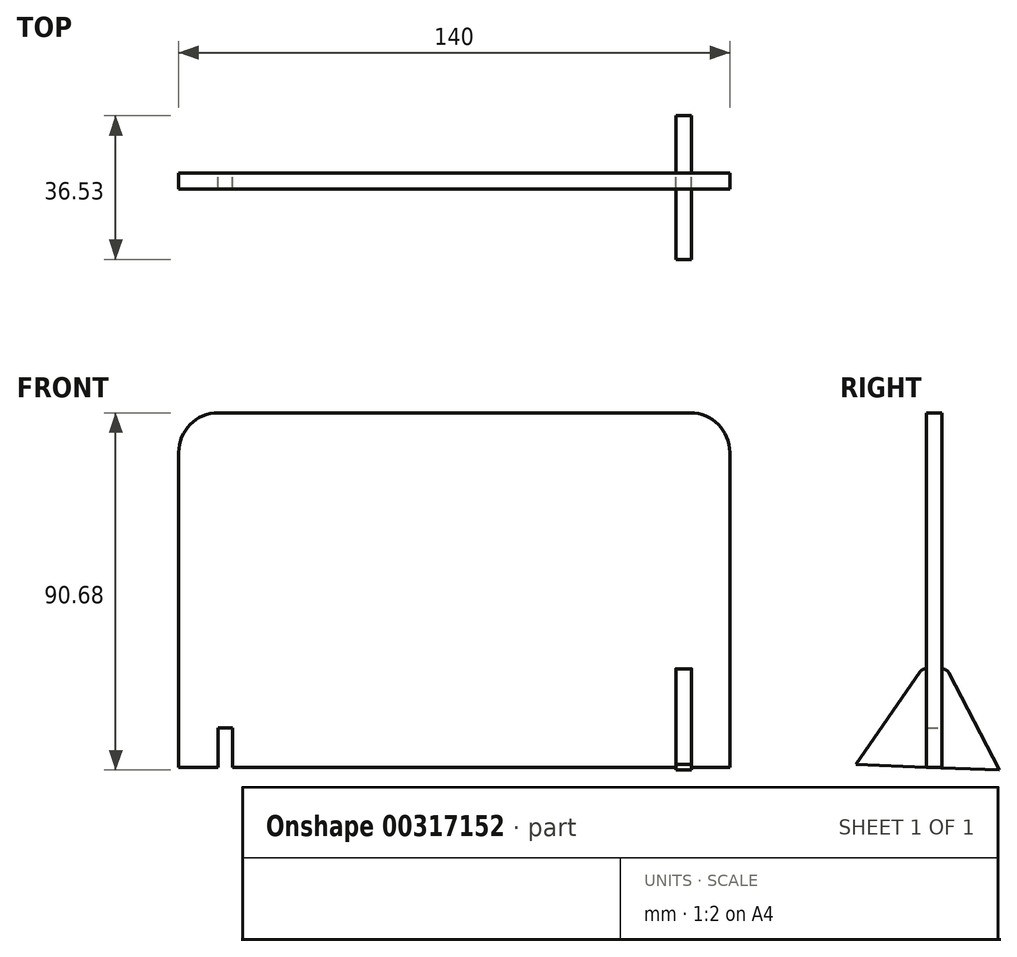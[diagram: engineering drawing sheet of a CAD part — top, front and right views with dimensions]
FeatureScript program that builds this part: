
annotation { "Feature Type Name" : "Feature", "Feature Type Description" : "" }
export const myFeature = defineFeature(function(context is Context, id is Id, definition is map)
    precondition{}
    {
        {
            var Q0;
            Q0=qCreatedBy(makeId("Front.planeOp"),FACE);
            var sketch = newSketch(context, id + "F0", { "sketchPlane" : qUnion([Q0])});
            skLineSegment(sketch, "E0.bottom", {"start": v(-60, 90) * mm, "end": v(60, 90) * mm});
            skLineSegment(sketch, "E0.top", {"start": v(-70, 0) * mm, "end": v(-60, 0) * mm});
            skLineSegment(sketch, "E0.left", {"start": v(-70, 80) * mm, "end": v(-70, 0) * mm});
            skLineSegment(sketch, "E0.right", {"start": v(70, 80) * mm, "end": v(70, 0) * mm});
            skPoint(sketch, "E1.visualSharp", {"position": v(-70, 90) * mm});
            skArc(sketch, "E1.filletArc", {"start": v(-60, 90) * mm, "mid": v(-67.07, 87.07) * mm, "end": v(-70, 80) * mm});
            skPoint(sketch, "E2.visualSharp", {"position": v(70, 90) * mm});
            skArc(sketch, "E2.filletArc", {"start": v(70, 80) * mm, "mid": v(67.07, 87.07) * mm, "end": v(60, 90) * mm});
            skLineSegment(sketch, "E3.top", {"start": v(-60, 10) * mm, "end": v(-56.3, 10) * mm});
            skLineSegment(sketch, "E3.left", {"start": v(-60, 0) * mm, "end": v(-60, 10) * mm});
            skLineSegment(sketch, "E3.right", {"start": v(-56.3, 0) * mm, "end": v(-56.3, 10) * mm});
            skLineSegment(sketch, "E4.MirrorCS", {"start": v(56.3, 0) * mm, "end": v(56.3, 10) * mm});
            skLineSegment(sketch, "E5.MirrorCS", {"start": v(60, 0) * mm, "end": v(60, 10) * mm});
            skLineSegment(sketch, "E6.MirrorCS", {"start": v(60, 10) * mm, "end": v(56.3, 10) * mm});
            skLineSegment(sketch, "E7.trimOffspring", {"start": v(60, 0) * mm, "end": v(70, 0) * mm});
            skLineSegment(sketch, "E8.trimOffspring", {"start": v(-56.3, 0) * mm, "end": v(56.3, 0) * mm});
            skSolve(sketch);
        }
        {
            var Q0;
            Q0 = qSketchRegion(id + "F0", true);
            extrude(context, id + "F1", {"entities" : qUnion([Q0]), "depth" : 4 * mm});
        }
        {
            var Q0;
            Q0=makeQuery(id+"F1.opExtrude","SWEPT_FACE",FACE,{"disambiguationData":[OSD([sQuery(id+"F0.wireOp",EDGE,"E4.MirrorCS")])]});
            var sketch = newSketch(context, id + "F2", { "sketchPlane" : qUnion([Q0])});
            skLineSegment(sketch, "E9.bottom", {"start": v(0, 10) * mm, "end": v(-4, 10) * mm});
            skLineSegment(sketch, "E10.left", {"start": v(-4, 10) * mm, "end": v(-4, 25) * mm});
            skLineSegment(sketch, "E10.right", {"start": v(0, 10) * mm, "end": v(0, 25) * mm});
            skLineSegment(sketch, "E11", {"start": v(-4, 25) * mm, "end": v(-4, 25) * mm});
            skLineSegment(sketch, "E12", {"start": v(-5.64, 24.14) * mm, "end": v(-21.9, 0.65) * mm});
            skLineSegment(sketch, "E13", {"start": v(0, 25) * mm, "end": v(0, 25) * mm});
            skLineSegment(sketch, "E14", {"start": v(1.77, 23.93) * mm, "end": v(14.63, -0.68) * mm});
            skLineSegment(sketch, "E15", {"start": v(14.63, -0.68) * mm, "end": v(-21.9, 0.65) * mm});
            skPoint(sketch, "E16.visualSharp", {"position": v(-5.05, 25) * mm});
            skArc(sketch, "E16.filletArc", {"start": v(-4, 25) * mm, "mid": v(-4.93, 24.77) * mm, "end": v(-5.64, 24.14) * mm});
            skPoint(sketch, "E17.visualSharp", {"position": v(1.21, 25) * mm});
            skArc(sketch, "E17.filletArc", {"start": v(1.77, 23.93) * mm, "mid": v(1.04, 24.71) * mm, "end": v(0, 25) * mm});
            skSolve(sketch);
        }
        {
            var Q0;
            Q0 = qSketchRegion(id + "F2", true);
            extrude(context, id + "F3", {"entities" : qUnion([Q0]), "operationType" : NewBodyOperationType.ADD, "depth" : 4 * mm});
        }
    });
